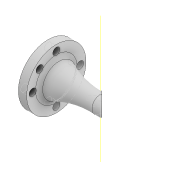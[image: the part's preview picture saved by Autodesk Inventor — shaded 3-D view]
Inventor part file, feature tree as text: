
AUTODESK INVENTOR PART (.ipt)
format: ipt  version: 2022 (Build 260153000, 153)  size: 456,704 bytes
history: native  units: mm
features: sketch x9, extrude x6, projected_geometry x5, revolve x1, plane x1, fillet x1, other x1
ambient origin geometry x8: Origin, YZ Plane, XZ Plane, XY Plane, X Axis, Y Axis, Z Axis, Center Point
bodies: Solid1 (feature_tree)
feature tree (24):
  extrude  "Extrusion1"  Depth=7.0mm TaperAngle=0.0deg
  sketch  "Sketch2"  dims[d9=15.0mm d11=7.0mm]
  revolve  "Revolution1"  [1 undecoded]
  sketch  "Sketch4"  dims[d14=37.0mm d16=45.0deg]
  plane  "Work Plane1"
  extrude  "Extrusion2"  Depth=73.0mm
  extrude  "Extrusion3"  TaperAngle=45.0deg  [1 undecoded]
  extrude  "Extrusion4"  Depth=10.0mm TaperAngle=0.0deg
  extrude  "Extrusion5"  Depth=20.0mm
  extrude  "Extrusion6"  Depth=3.0mm
  fillet  "Fillet1"  Radius=3.0mm
  sketch  "Sketch1"  dims[d1=30.0mm d2=20.0mm d3=90.0deg d4=6.0mm d5=90.0deg d6=135.0deg d7=7.0mm d8=0.0mm]
  sketch  "Sketch3"  dims[d12=360.0deg d13=73.0mm]
  other  "Work Axis1"
  sketch  "Sketch5"  dims[d17=10.0mm d18=0.0mm d19=10.0mm d20=0.0mm]
  projected_geometry  "Projected Loop1"
  sketch  "Sketch6"  dims[d21=40.0mm d22=20.0mm]
  projected_geometry  "Projected Loop2"
  sketch  "Sketch7"  dims[d23=0.0mm d24=3.0mm d25=3.0mm]
  projected_geometry  "Projected Loop3"
  sketch  "Sketch8"  dims[d26=3.0mm]
  projected_geometry  "Projected Loop4"
  sketch  "Sketch9"  dims[d27=4.0mm d28=6.0mm d29=5.0mm d30=0.0mm d31=3.0mm d32=0.0mm d33=1.0mm d34=0.0mm d35=4.0mm d36=0.0mm d37=0.0mm d38=0.0mm]
  projected_geometry  "Projected Loop5"
note: 2 required parameter values undecoded (feature->parameter linkage not recoverable at this tier; creation-order binding heuristic only, values carry confidence <= 0.55)